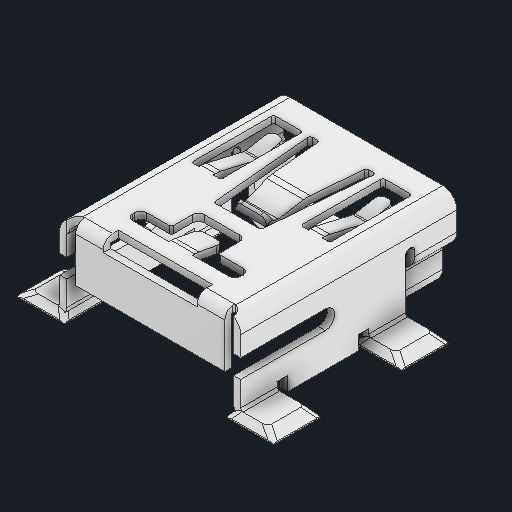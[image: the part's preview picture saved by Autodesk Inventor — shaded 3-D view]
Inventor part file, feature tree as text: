
AUTODESK INVENTOR PART (.ipt)
format: ipt  version: 2023 (Build 270158000, 158)  size: 381,440 bytes
history: native  units: in
note: dims shown in document units (in); Inventor stores cm internally (conversion verified against a paired STEP export)
features: fillet x1
ambient origin geometry x8: Origin, YZ Plane, XZ Plane, XY Plane, X Axis, Y Axis, Z Axis, Center Point
bodies: Solid1 (feature_tree)
feature tree (1):
  fillet  "Fillet14"  [1 undecoded]
note: 1 required parameter value undecoded (feature->parameter linkage not recoverable at this tier; creation-order binding heuristic only, values carry confidence <= 0.55)
